# Revit family: CONV_Flokk_OffcChrs_RHNewLogic220
name_source: partatom
category: Furniture
revit_build: Autodesk Revit 2017 (Build: 20181011_1645(x64)
units: mm (PartAtom-declared; Revit-internal decimal feet)

## family parameters
Always vertical = Yes
Cut with Voids When Loaded = No
OmniClass Number = 23.40.20.14.14.11
OmniClass Title = Chairs
Room Calculation Point = No
Shared = No
Work Plane-Based = No

## types (1)
- RH New Logic 220
    AssetType = Movable
    BIMObjectName = CONV_Flokk_OffcChrs_RHNewLogic220
    Brand = RH
    Category = Task chairs
    Collection = RH New Logic
    Color = Various
    Cost = 0 $
    Description = RH New Logic 220 has a high back, comes as standard with castors for soft floor and base in black aluminum. It can be enhanced with a wide range of options such as neck rest, armrest, uniformed upholstery and decorative stitching. It is also available with XL seat.
    Designer = StokkeAustad
    DurationUnit = Year
    Features = Adjustable seat height, armrest, headrest
    Finish = Black aluminum
    HighestSeatingHeight = 550 mm
    IfcExportAs = IfcFurnishingElementType
    IfcExportType = CHAIR
    LowestSeatingHeight = 410 mm  [stored 1.34514 ft]
    MainColor = Various
    Manufacturer = Flokk
    ManufacturerName = Flokk
    ManufacturerURL = https://www.flokk.com
    Material = Textile, metal, plastic
    Model = RH New Logic 220
    ModelNumber = 9212
    NBSDescription = Office chairs
    NBSReference = 45-35-20/330
    Name = OffcChrs_RHNewLogic220
    NominalDepth = 725 mm  [stored 2.37861 ft]
    NominalLength = 780 mm  [stored 2.55906 ft]
    OfficeChairSecondaryMaterial = Plastic, Opaque Black
    OffieChairTertiaryMaterial = Black Metal
    ProductInformation = RH Mereo 200 has a medium back and comes as standard with castors for carpeted floors and base in grey lacquered aluminium. It can also be enhanced with a range of options such as armrests and coat hanger.
    SeatingHeight = 500 mm  [stored 1.64042 ft]
    Shape = Sculptured
    Size = 650x650x1108/1188 mm
    URL = https://www.flokk.com
    Uniclass2 = Pr_40_50_12_57
    Uniclass2015Description = Office chairs
    Uniclass2015Reference = Pr_40_50_12_57
    Version = 1
    VersionDate = 18/04/2019
    WarrantyDurationUnit = Year
    Weight = 29 kg.

note: [stored X ft] marks values corroborated as IEEE doubles in the binary element streams (Revit-internal decimal feet)

## geometry (parser evidence)
native form markers: Sweep x11
no freeform markers — native parametric forms only
